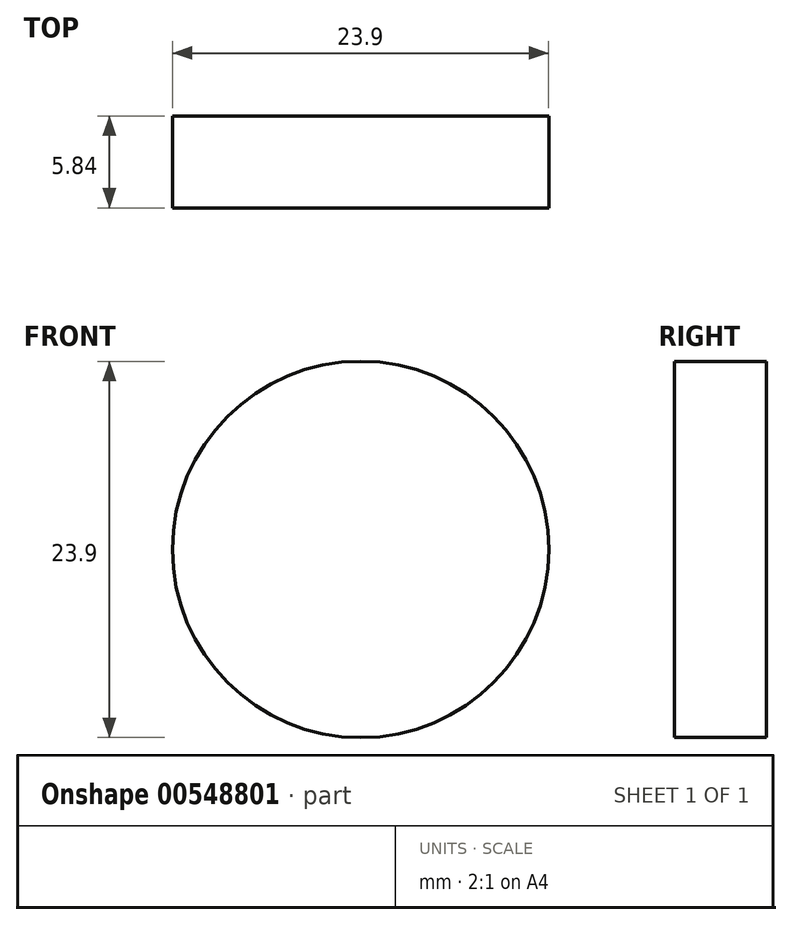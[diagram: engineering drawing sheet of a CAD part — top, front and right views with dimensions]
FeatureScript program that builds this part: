
annotation { "Feature Type Name" : "Feature", "Feature Type Description" : "" }
export const myFeature = defineFeature(function(context is Context, id is Id, definition is map)
    precondition{}
    {
        {
            var Q0;
            Q0=qCreatedBy(makeId("Front.planeOp"),FACE);
            var sketch = newSketch(context, id + "F0", { "sketchPlane" : qUnion([Q0])});
            skCircle(sketch, "E0", {"center": v(46.26, -8.54) * mm, "radius": 11.95 * mm});
            skSolve(sketch);
        }
        {
            var Q0;
            Q0=makeQuery(id+"F0.imprint","IMPRINT",FACE,{"disambiguationData":[TD([[makeQuery(id+"F0.imprint","IMPRINT",EDGE,{"derivedFrom":sQuery(id+"F0.wireOp",EDGE,"E0")}),1.0]])]});
            extrude(context, id + "F1", {"entities" : qUnion([Q0]), "depth" : 5.84 * mm, "offsetDistance" : 25.4 * mm});
        }
    });
